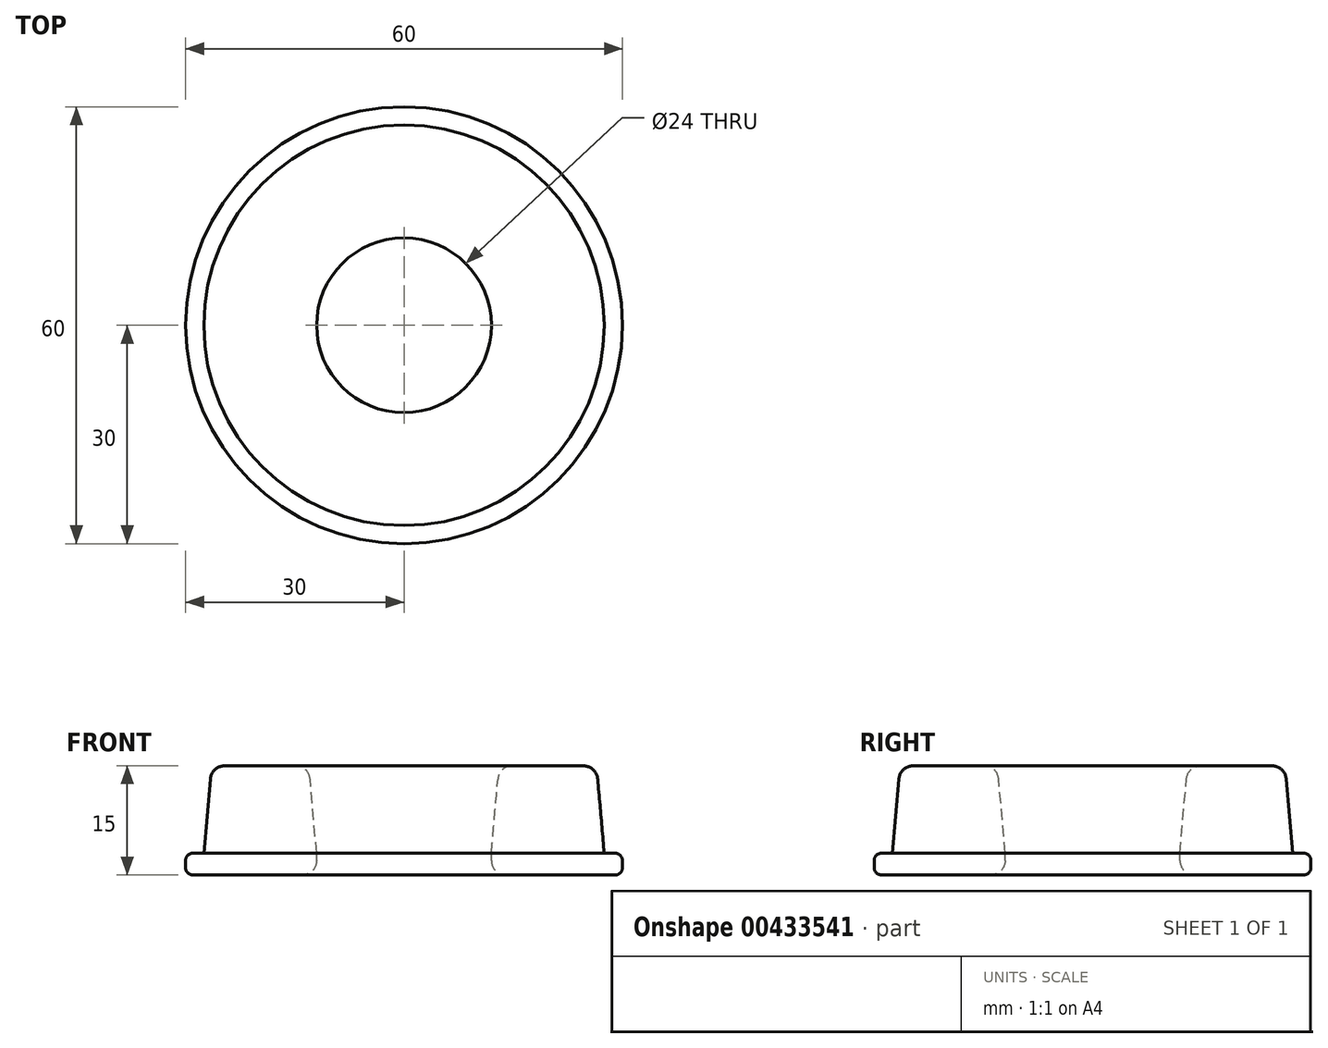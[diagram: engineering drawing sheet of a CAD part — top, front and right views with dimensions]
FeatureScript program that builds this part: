
annotation { "Feature Type Name" : "Feature", "Feature Type Description" : "" }
export const myFeature = defineFeature(function(context is Context, id is Id, definition is map)
    precondition{}
    {
        {
            var Q0;
            Q0=qCreatedBy(makeId("Top.planeOp"),FACE);
            var sketch = newSketch(context, id + "F0", { "sketchPlane" : qUnion([Q0])});
            skCircle(sketch, "E0", {"center": v(0, 0) * mm, "radius": 12 * mm});
            skCircle(sketch, "E1", {"center": v(0, 0) * mm, "radius": 27.5 * mm});
            skCircle(sketch, "E2", {"center": v(0, 0) * mm, "radius": 27.25 * mm, "construction": true});
            skSolve(sketch);
        }
        {
            var Q0;
            Q0 = qSketchRegion(id + "F0", true);
            extrude(context, id + "F1", {"entities" : qUnion([Q0]), "depth" : 12 * mm, "hasDraft" : true, "draftAngle" : 5 * degree, "draftPullDirection" : true});
        }
        {
            var Q0;
            Q0=qCreatedBy(makeId("Top.planeOp"),FACE);
            var sketch = newSketch(context, id + "F2", { "sketchPlane" : qUnion([Q0])});
            skCircle(sketch, "E3", {"center": v(0, 0) * mm, "radius": 30 * mm});
            skCircle(sketch, "E4", {"center": v(0, 0) * mm, "radius": 12 * mm});
            skSolve(sketch);
        }
        {
            var Q0;
            Q0 = qSketchRegion(id + "F2", true);
            extrude(context, id + "F3", {"entities" : qUnion([Q0]), "operationType" : NewBodyOperationType.ADD, "oppositeDirection" : true, "depth" : 3 * mm});
        }
        {
            var Q0;
            Q0=makeQuery(id+"F1.opExtrude","CAP_EDGE",EDGE,{"disambiguationData":[OSD([sQuery(id+"F0.wireOp",EDGE,"E1")])],"isStart":false});
            var Q1;
            Q1=makeQuery(id+"F3.opExtrude","CAP_EDGE",EDGE,{"disambiguationData":[OSD([sQuery(id+"F2.wireOp",EDGE,"E4")])],"isStart":false});
            var Q2;
            Q2=makeQuery(id+"F1.opExtrude","CAP_EDGE",EDGE,{"disambiguationData":[OSD([sQuery(id+"F0.wireOp",EDGE,"E0")])],"isStart":false});
            fillet(context, id + "F4", {"entities" : qUnion([Q0, Q1, Q2]), "radius" : 2 * mm, "tangentPropagation" : true, "allowEdgeOverflow" : false});
        }
        {
            var Q0;
            Q0=makeQuery(id+"F3.opExtrude","CAP_EDGE",EDGE,{"disambiguationData":[OSD([sQuery(id+"F2.wireOp",EDGE,"E3")])],"isStart":false});
            var Q1;
            Q1=makeQuery(id+"F3.opExtrude","CAP_EDGE",EDGE,{"disambiguationData":[OSD([sQuery(id+"F2.wireOp",EDGE,"E3")])],"isStart":true});
            fillet(context, id + "F5", {"entities" : qUnion([Q0, Q1]), "radius" : 1 * mm, "tangentPropagation" : true, "allowEdgeOverflow" : false});
        }
    });
